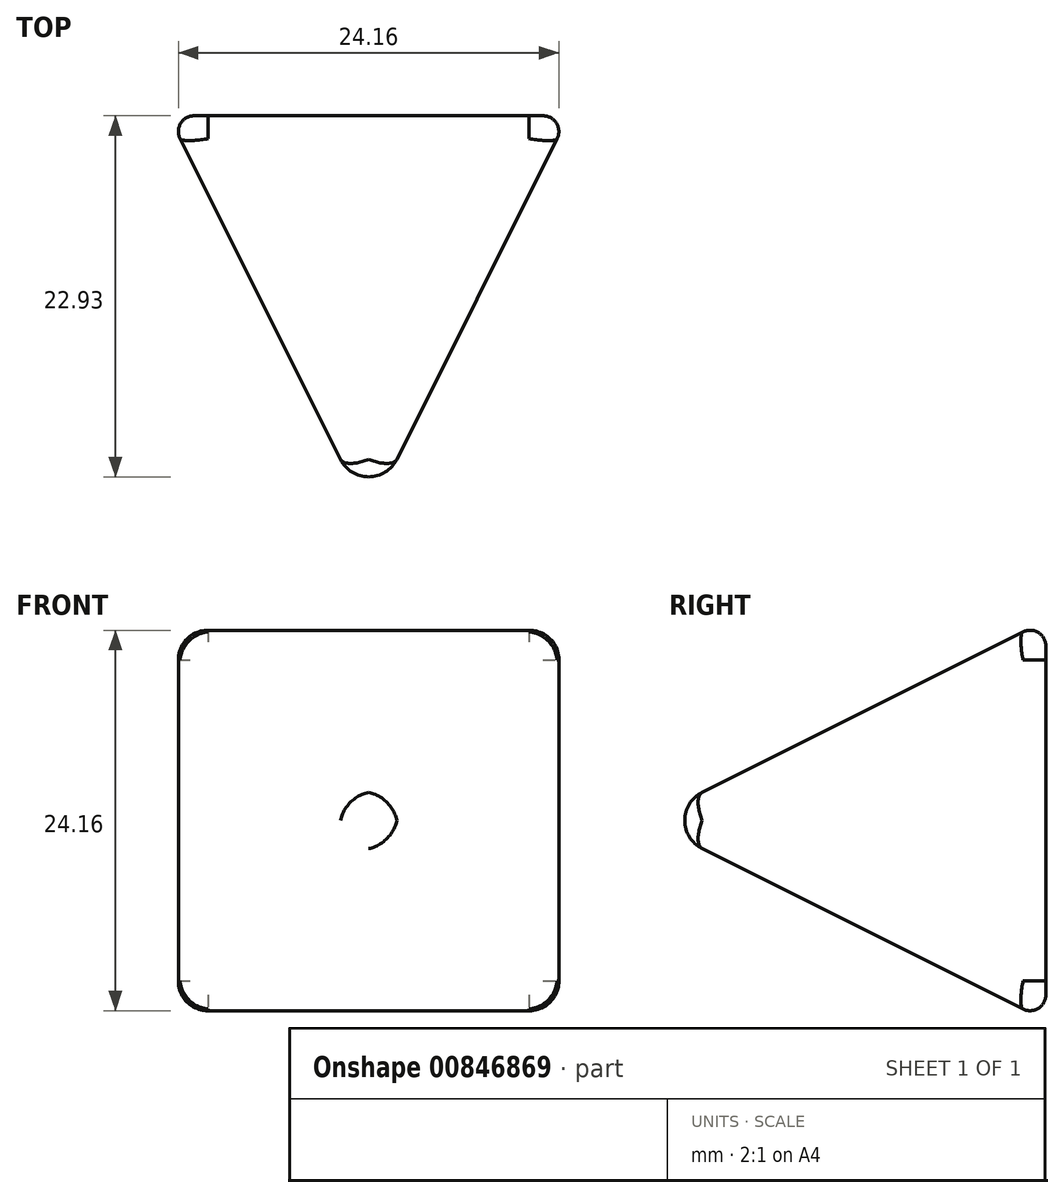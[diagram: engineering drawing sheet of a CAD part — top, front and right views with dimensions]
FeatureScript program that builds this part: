
annotation { "Feature Type Name" : "Feature", "Feature Type Description" : "" }
export const myFeature = defineFeature(function(context is Context, id is Id, definition is map)
    precondition{}
    {
        {
            var Q0;
            Q0=qCreatedBy(makeId("Front.planeOp"),FACE);
            var sketch = newSketch(context, id + "F0", { "sketchPlane" : qUnion([Q0])});
            skLineSegment(sketch, "E0.bottom", {"start": v(12.7, -12.7) * mm, "end": v(-12.7, -12.7) * mm});
            skLineSegment(sketch, "E0.top", {"start": v(12.7, 12.7) * mm, "end": v(-12.7, 12.7) * mm});
            skLineSegment(sketch, "E0.left", {"start": v(12.7, -12.7) * mm, "end": v(12.7, 12.7) * mm});
            skLineSegment(sketch, "E0.right", {"start": v(-12.7, -12.7) * mm, "end": v(-12.7, 12.7) * mm});
            skPoint(sketch, "E0.middle", {"position": v(0, 0) * mm});
            skSolve(sketch);
        }
        {
            var Q0;
            Q0=qCreatedBy(makeId("Right.planeOp"),FACE);
            var sketch = newSketch(context, id + "F1", { "sketchPlane" : qUnion([Q0])});
            skLineSegment(sketch, "E1", {"start": v(0, 0) * mm, "end": v(-25.4, 0) * mm, "construction": true});
            skPoint(sketch, "E2", {"position": v(-25.4, 0) * mm});
            skSolve(sketch);
        }
        {
            var Q0;
            Q0=makeQuery(id+"F0.imprint","IMPRINT",FACE,{"disambiguationData":[TD([[makeQuery(id+"F0.imprint","IMPRINT",EDGE,{"derivedFrom":sQuery(id+"F0.wireOp",EDGE,"E0.bottom")}),-1.0]])]});
            var Q1;
            Q1=sQuery(id+"F1.wireOp",VERTEX,"E2");
            loft(context, id + "F2", {"sheetProfilesArray" : [{ "sheetProfileEntities" : qUnion([Q0]) }, { "sheetProfileEntities" : qUnion([Q1]) }]});
        }
        {
            var Q0;
            Q0=makeQuery(id+"F2.opLoft","SWEPT_EDGE",EDGE,{"disambiguationData":[OSD([sQuery(id+"F0.wireOp",EDGE,"E0.bottom"),sQuery(id+"F0.wireOp",EDGE,"E0.right"),sQuery(id+"F1.wireOp",VERTEX,"E2")])]});
            var Q1;
            Q1=makeQuery(id+"F2.opLoft","SWEPT_EDGE",EDGE,{"disambiguationData":[OSD([sQuery(id+"F0.wireOp",EDGE,"E0.bottom"),sQuery(id+"F0.wireOp",EDGE,"E0.left"),sQuery(id+"F1.wireOp",VERTEX,"E2")])]});
            var Q2;
            Q2=makeQuery(id+"F2.opLoft","SWEPT_EDGE",EDGE,{"disambiguationData":[OSD([sQuery(id+"F0.wireOp",EDGE,"E0.top"),sQuery(id+"F0.wireOp",EDGE,"E0.left"),sQuery(id+"F1.wireOp",VERTEX,"E2")])]});
            var Q3;
            Q3=makeQuery(id+"F2.opLoft","SWEPT_EDGE",EDGE,{"disambiguationData":[OSD([sQuery(id+"F0.wireOp",EDGE,"E0.top"),sQuery(id+"F0.wireOp",EDGE,"E0.right"),sQuery(id+"F1.wireOp",VERTEX,"E2")])]});
            fillet(context, id + "F3", {"entities" : qUnion([Q0, Q1, Q2, Q3]), "radius" : 2 * mm, "tangentPropagation" : true, "allowEdgeOverflow" : false});
        }
        {
            var Q0;
            Q0=makeQuery(id+"F2.opLoft","MID_CAP_EDGE",EDGE,{"disambiguationData":[OSD([sQuery(id+"F0.wireOp",EDGE,"E0.bottom"),sQuery(id+"F0.wireOp",EDGE,"E0.left"),sQuery(id+"F0.wireOp",EDGE,"E0.right")])],"capPos":0.0});
            var Q1;
            Q1=makeQuery(id+"F2.opLoft","MID_CAP_EDGE",EDGE,{"disambiguationData":[OSD([sQuery(id+"F0.wireOp",EDGE,"E0.bottom"),sQuery(id+"F0.wireOp",EDGE,"E0.top"),sQuery(id+"F0.wireOp",EDGE,"E0.right")])],"capPos":0.0});
            var Q2;
            Q2=makeQuery(id+"F2.opLoft","MID_CAP_EDGE",EDGE,{"disambiguationData":[OSD([sQuery(id+"F0.wireOp",EDGE,"E0.bottom"),sQuery(id+"F0.wireOp",EDGE,"E0.top"),sQuery(id+"F0.wireOp",EDGE,"E0.left")])],"capPos":0.0});
            var Q3;
            Q3=makeQuery(id+"F2.opLoft","MID_CAP_EDGE",EDGE,{"disambiguationData":[OSD([sQuery(id+"F0.wireOp",EDGE,"E0.top"),sQuery(id+"F0.wireOp",EDGE,"E0.left"),sQuery(id+"F0.wireOp",EDGE,"E0.right")])],"capPos":0.0});
            fillet(context, id + "F4", {"entities" : qUnion([Q0, Q1, Q2, Q3]), "radius" : 1 * mm, "tangentPropagation" : true, "allowEdgeOverflow" : false});
        }
    });
